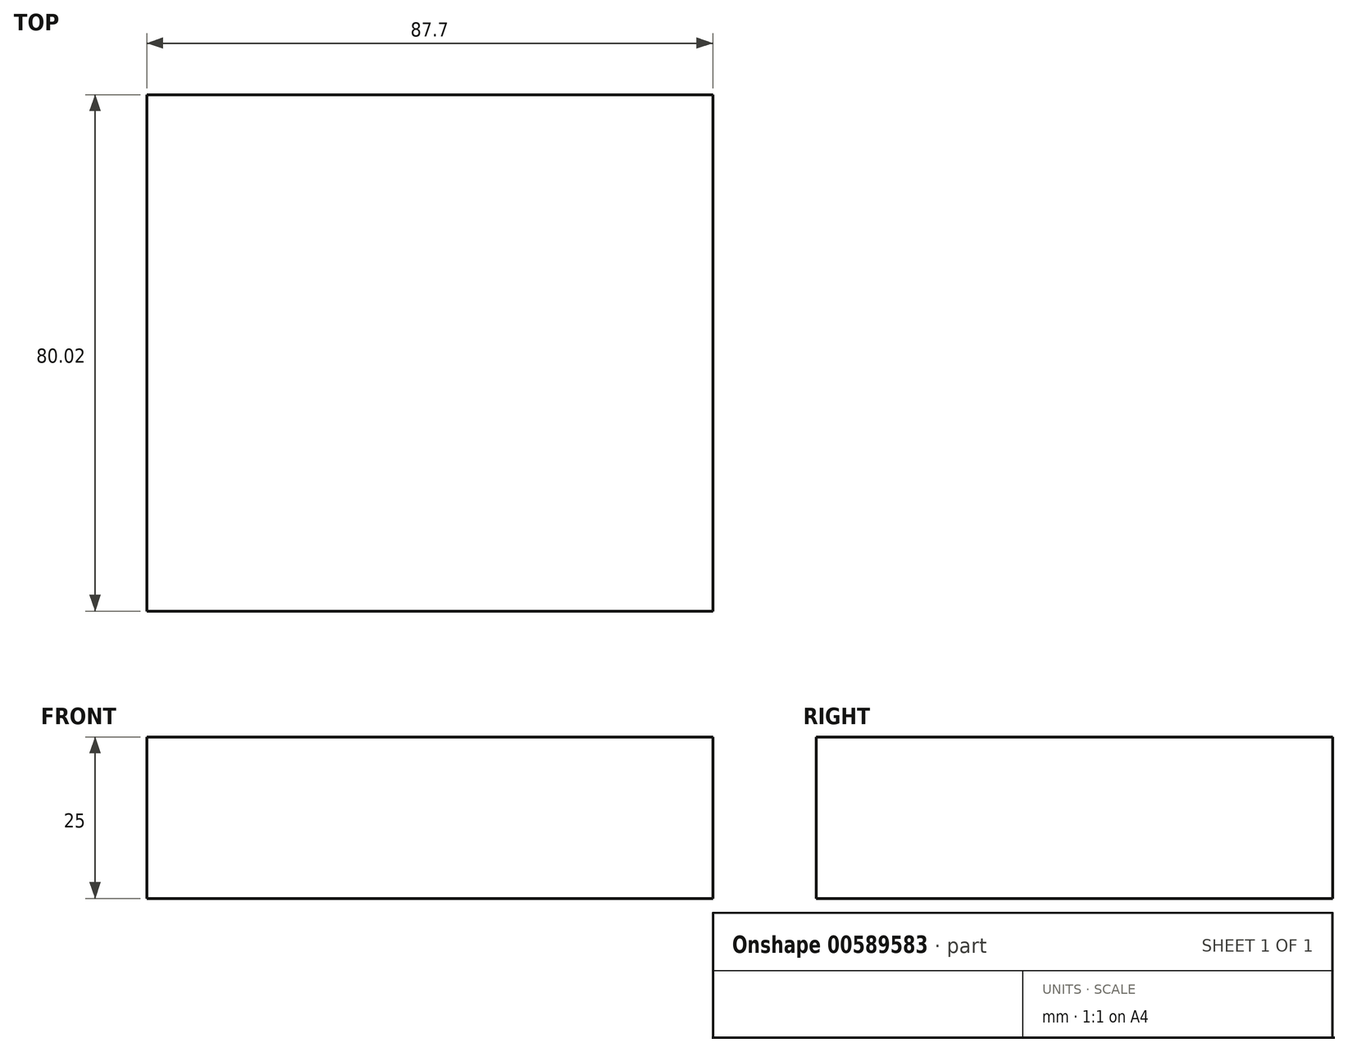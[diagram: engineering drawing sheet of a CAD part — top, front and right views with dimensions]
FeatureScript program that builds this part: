
annotation { "Feature Type Name" : "Feature", "Feature Type Description" : "" }
export const myFeature = defineFeature(function(context is Context, id is Id, definition is map)
    precondition{}
    {
        {
            var Q0;
            Q0=qCreatedBy(makeId("Top.planeOp"),FACE);
            var sketch = newSketch(context, id + "F0", { "sketchPlane" : qUnion([Q0])});
            skLineSegment(sketch, "E0.bottom", {"start": v(-152.82, 36.52) * mm, "end": v(-65.12, 36.52) * mm});
            skLineSegment(sketch, "E0.top", {"start": v(-152.82, -43.5) * mm, "end": v(-65.12, -43.5) * mm});
            skLineSegment(sketch, "E0.left", {"start": v(-152.82, 36.52) * mm, "end": v(-152.82, -43.5) * mm});
            skLineSegment(sketch, "E0.right", {"start": v(-65.12, 36.52) * mm, "end": v(-65.12, -43.5) * mm});
            skSolve(sketch);
        }
        {
            var Q0;
            Q0=makeQuery(id+"F0.imprint","IMPRINT",FACE,{"disambiguationData":[TD([[makeQuery(id+"F0.imprint","IMPRINT",EDGE,{"derivedFrom":sQuery(id+"F0.wireOp",EDGE,"E0.bottom")}),-1.0]])]});
            extrude(context, id + "F1", {"entities" : qUnion([Q0]), "depth" : 25 * mm, "offsetDistance" : 25 * mm});
        }
    });
